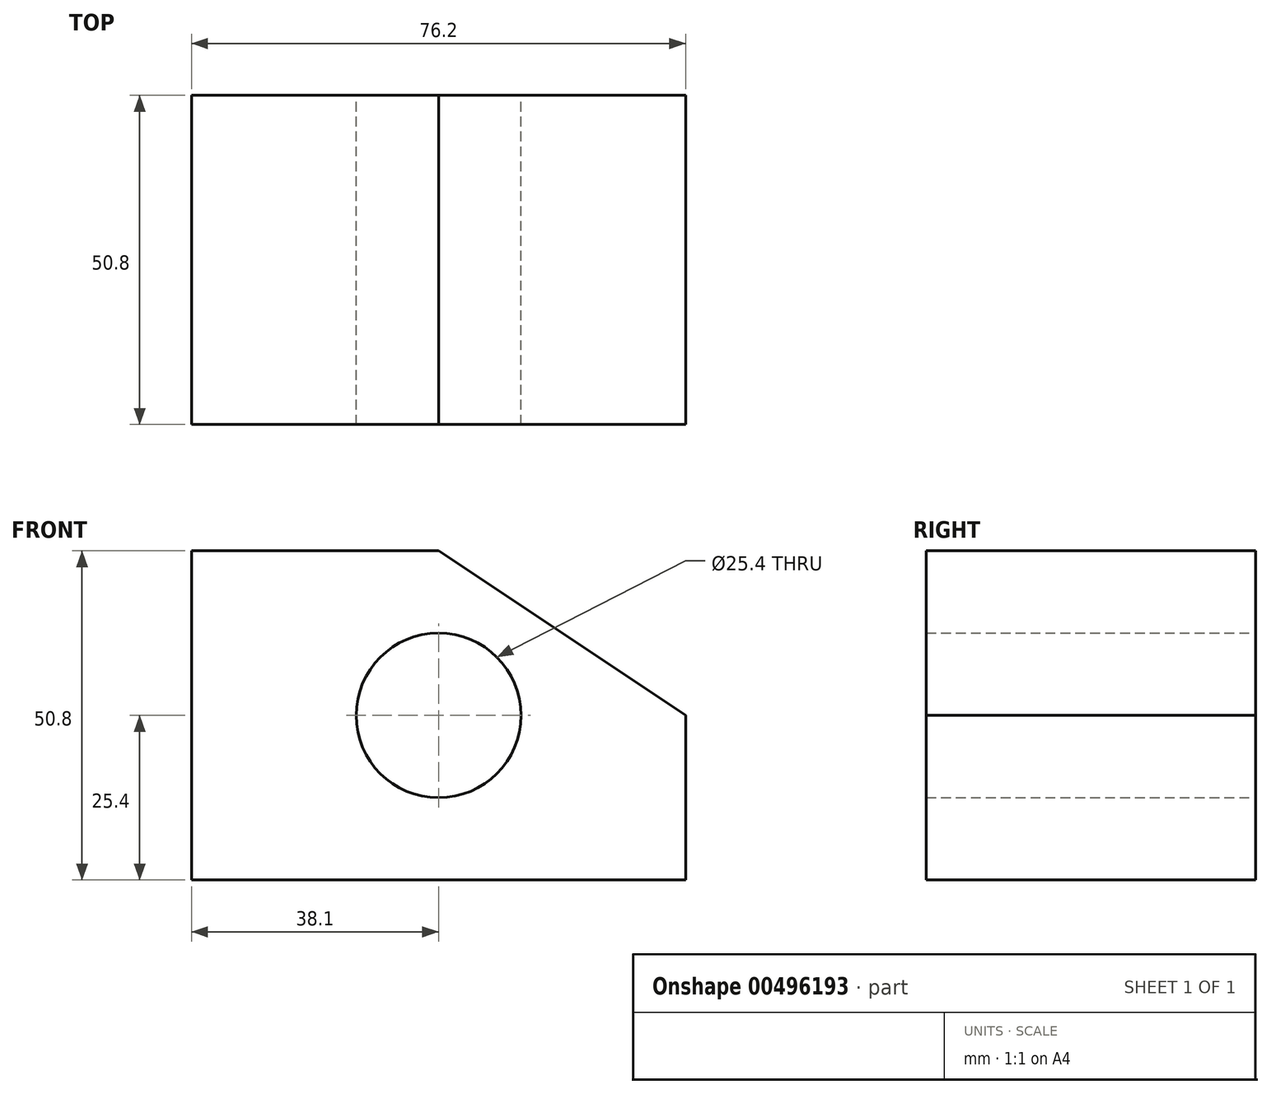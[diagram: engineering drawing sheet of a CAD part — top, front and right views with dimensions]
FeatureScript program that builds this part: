
annotation { "Feature Type Name" : "Feature", "Feature Type Description" : "" }
export const myFeature = defineFeature(function(context is Context, id is Id, definition is map)
    precondition{}
    {
        {
            var Q0;
            Q0=qCreatedBy(makeId("Front.planeOp"),FACE);
            var sketch = newSketch(context, id + "F0", { "sketchPlane" : qUnion([Q0])});
            skLineSegment(sketch, "E0.bottom", {"start": v(-38.1, 25.4) * mm, "end": v(0, 25.4) * mm});
            skLineSegment(sketch, "E0.top", {"start": v(-38.1, -25.4) * mm, "end": v(38.1, -25.4) * mm});
            skLineSegment(sketch, "E0.left", {"start": v(-38.1, 25.4) * mm, "end": v(-38.1, -25.4) * mm});
            skLineSegment(sketch, "E0.right", {"start": v(38.1, 0) * mm, "end": v(38.1, -25.4) * mm});
            skCircle(sketch, "E1", {"center": v(0, 0) * mm, "radius": 12.7 * mm});
            skLineSegment(sketch, "E2", {"start": v(0, 25.4) * mm, "end": v(38.1, 0) * mm});
            skSolve(sketch);
        }
        {
            var Q0;
            Q0=makeQuery(id+"F0.imprint","IMPRINT",FACE,{"disambiguationData":[TD([[makeQuery(id+"F0.imprint","IMPRINT",EDGE,{"derivedFrom":sQuery(id+"F0.wireOp",EDGE,"E0.bottom")}),-1.0]])]});
            extrude(context, id + "F1", {"entities" : qUnion([Q0]), "depth" : 50.8 * mm});
        }
    });
